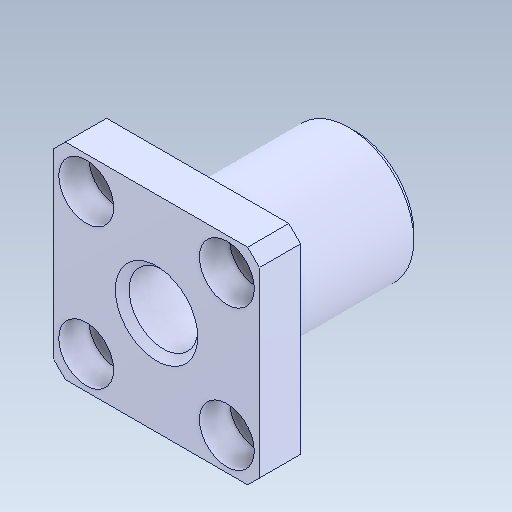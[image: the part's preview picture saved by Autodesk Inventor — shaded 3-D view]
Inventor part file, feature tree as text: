
AUTODESK INVENTOR PART (.ipt)
format: ipt  version: 2020 (Build 240168000, 168)  size: 151,552 bytes
history: native  units: in
note: dims shown in document units (in); Inventor stores cm internally (conversion verified against a paired STEP export)
features: chamfer x1
ambient origin geometry x8: Origin, YZ Plane, XZ Plane, XY Plane, X Axis, Y Axis, Z Axis, Center Point
bodies: Solid1 (feature_tree)
feature tree (1):
  chamfer  "Chamfer1"  [1 undecoded]
note: 1 required parameter value undecoded (feature->parameter linkage not recoverable at this tier; creation-order binding heuristic only, values carry confidence <= 0.55)
